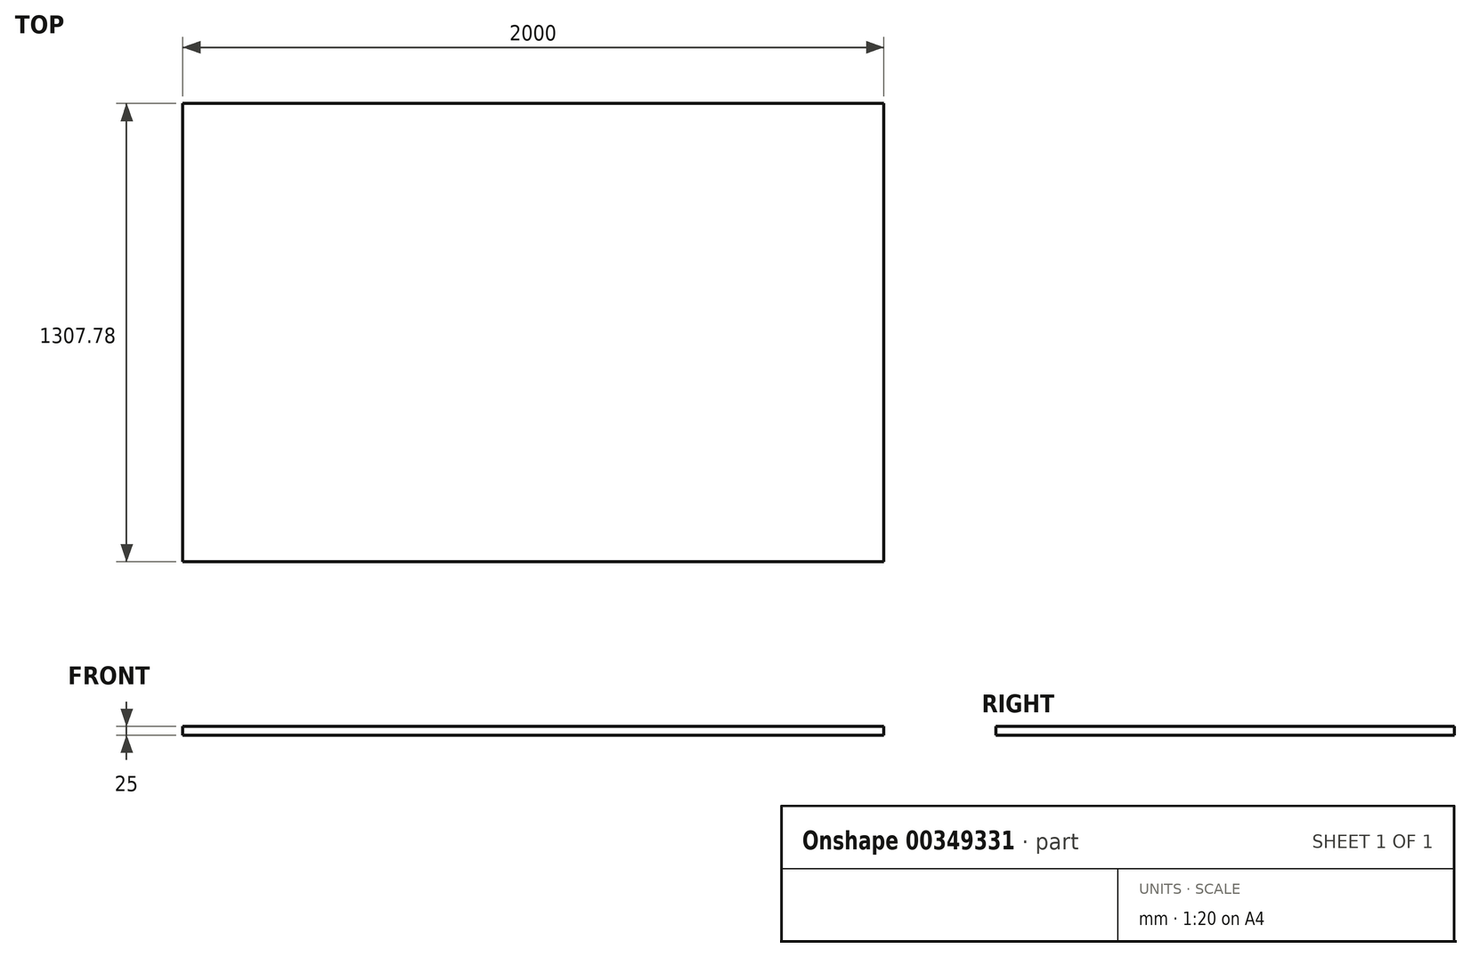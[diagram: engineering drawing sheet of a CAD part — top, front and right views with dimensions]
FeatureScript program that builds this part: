
annotation { "Feature Type Name" : "Feature", "Feature Type Description" : "" }
export const myFeature = defineFeature(function(context is Context, id is Id, definition is map)
    precondition{}
    {
        {
            var Q0;
            Q0=qCreatedBy(makeId("Top.planeOp"),FACE);
            var sketch = newSketch(context, id + "F0", { "sketchPlane" : qUnion([Q0])});
            skLineSegment(sketch, "E0.bottom", {"start": v(1000, -653.89) * mm, "end": v(-1000, -653.89) * mm});
            skLineSegment(sketch, "E0.top", {"start": v(1000, 653.89) * mm, "end": v(-1000, 653.89) * mm});
            skLineSegment(sketch, "E0.left", {"start": v(1000, -653.89) * mm, "end": v(1000, 653.89) * mm});
            skLineSegment(sketch, "E0.right", {"start": v(-1000, -653.89) * mm, "end": v(-1000, 653.89) * mm});
            skPoint(sketch, "E0.middle", {"position": v(0, 0) * mm});
            skSolve(sketch);
        }
        {
            var Q0;
            Q0=makeQuery(id+"F0.imprint","IMPRINT",FACE,{"disambiguationData":[TD([[makeQuery(id+"F0.imprint","IMPRINT",EDGE,{"derivedFrom":sQuery(id+"F0.wireOp",EDGE,"E0.bottom")}),-1.0]])]});
            extrude(context, id + "F1", {"entities" : qUnion([Q0]), "endBound" : BoundingType.SYMMETRIC, "depth" : 25 * mm});
        }
    });
